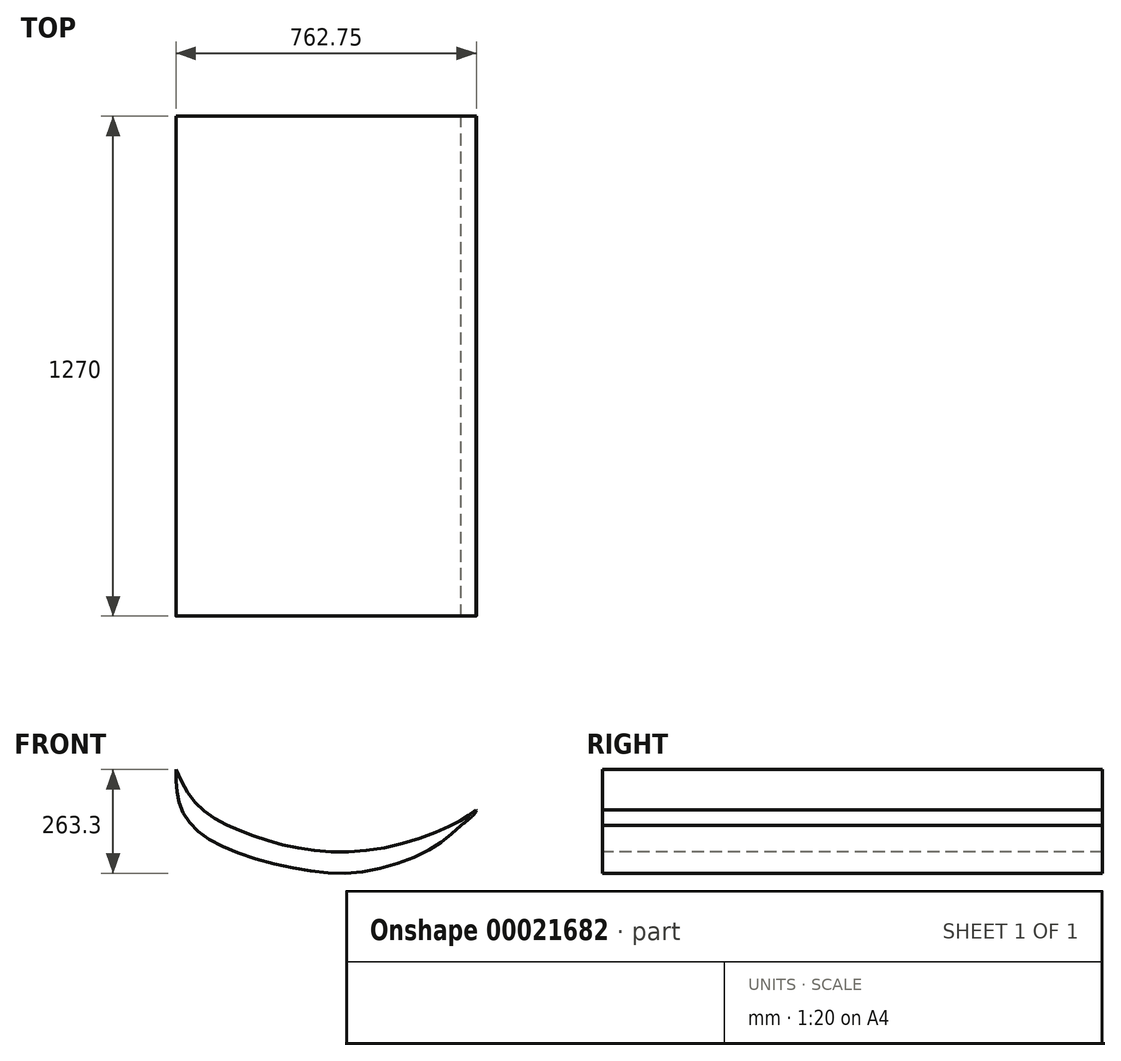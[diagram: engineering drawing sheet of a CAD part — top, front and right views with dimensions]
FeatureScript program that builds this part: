
annotation { "Feature Type Name" : "Feature", "Feature Type Description" : "" }
export const myFeature = defineFeature(function(context is Context, id is Id, definition is map)
    precondition{}
    {
        {
            var Q0;
            Q0=qCreatedBy(makeId("Front.planeOp"),FACE);
            var sketch = newSketch(context, id + "F0", { "sketchPlane" : qUnion([Q0])});
            skFitSpline(sketch, "E0", {"points": [v(-364.52, 115.85) * mm, v(-360.53, 46.04) * mm, v(-330.6, -17.8) * mm, v(-246.83, -79.63) * mm, v(-61.32, -135.49) * mm, v(110.23, -143.46) * mm, v(275.8, -89.6) * mm, v(359.58, -25.77) * mm], "startDerivative": vector(-9.46, -655.89) * mm, "endDerivative": vector(552.65, 501.54) * mm});
            skFitSpline(sketch, "E1", {"points": [v(-364.52, 115.85) * mm, v(-196.96, 46.04) * mm, v(-23.42, 10.13) * mm, v(217.95, -7.82) * mm, v(397.48, 14.12) * mm, v(359.58, -25.77) * mm], "startDerivative": vector(781.81, -369.32) * mm, "endDerivative": vector(-539.9, -433.38) * mm});
            skFitSpline(sketch, "E2", {"points": [v(-364.52, 115.85) * mm, v(-308.97, 24.1) * mm, v(-204.94, -37.74) * mm, v(-53.34, -83.62) * mm, v(148.13, -85.62) * mm, v(335.17, -25.77) * mm, v(397.48, 14.12) * mm], "startDerivative": vector(314.13, -679.9) * mm, "endDerivative": vector(428.24, 319.78) * mm});
            skSolve(sketch);
        }
        {
            var Q0;
            {var subQ2=sQuery(id+"F0.wireOp",EDGE,"E0");Q0=makeQuery(id+"F0.imprint","IMPRINT",FACE,{"disambiguationData":[TD([[makeQuery(id+"F0.imprint","IMPRINT",EDGE,{"derivedFrom":subQ2}),1.0]])]});}
            extrude(context, id + "F1", {"entities" : qUnion([Q0]), "depth" : 1270 * mm});
        }
    });
